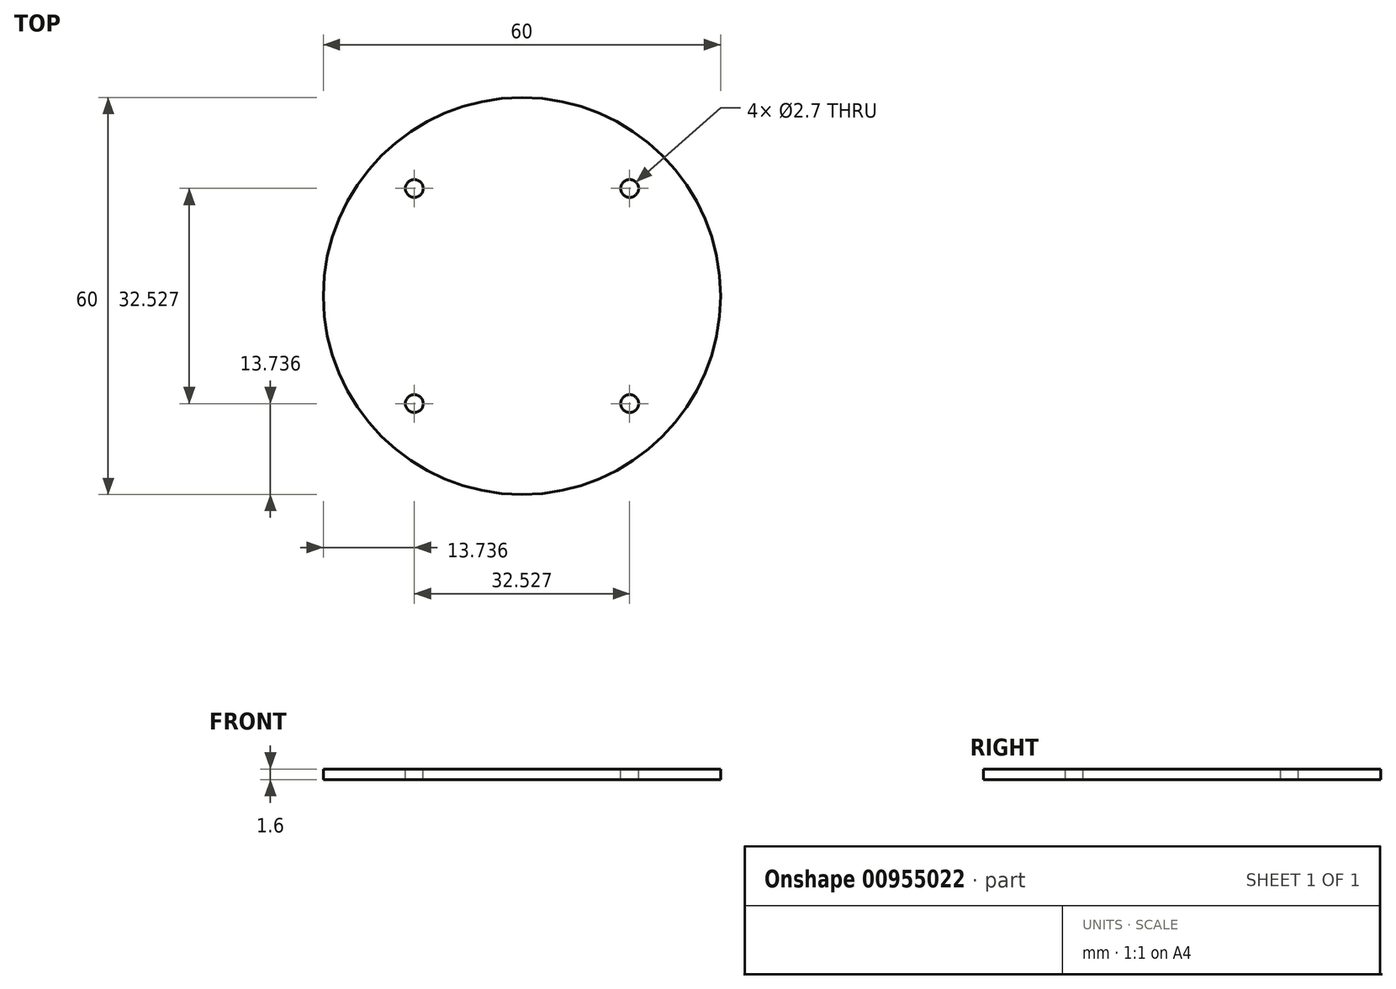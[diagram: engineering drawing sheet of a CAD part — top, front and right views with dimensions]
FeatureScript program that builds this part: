
annotation { "Feature Type Name" : "Feature", "Feature Type Description" : "" }
export const myFeature = defineFeature(function(context is Context, id is Id, definition is map)
    precondition{}
    {
        {
            var Q0;
            Q0=qCreatedBy(makeId("Top.planeOp"),FACE);
            var sketch = newSketch(context, id + "F0", { "sketchPlane" : qUnion([Q0])});
            skCircle(sketch, "E0", {"center": v(0, 0) * mm, "radius": 30 * mm});
            skSolve(sketch);
        }
        {
            var Q0;
            Q0 = qSketchRegion(id + "F0", true);
            extrude(context, id + "F1", {"entities" : qUnion([Q0]), "depth" : 1.6 * mm, "offsetDistance" : 25.4 * mm});
        }
        {
            var Q0;
            Q0=makeQuery(id+"F1.opExtrude","CAP_FACE",FACE,{"disambiguationData":[OSD([sQuery(id+"F0.wireOp",EDGE,"E0")])],"isStart":false});
            var sketch = newSketch(context, id + "F2", { "sketchPlane" : qUnion([Q0])});
            skCircle(sketch, "E1", {"center": v(-16.26, 16.26) * mm, "radius": 1.35 * mm});
            skLineSegment(sketch, "E2", {"start": v(0, 0) * mm, "end": v(-36.01, 36.01) * mm, "construction": true});
            skCircle(sketch, "E3.1.0", {"center": v(-16.26, -16.26) * mm, "radius": 1.35 * mm});
            skCircle(sketch, "E3.2.0", {"center": v(16.26, -16.26) * mm, "radius": 1.35 * mm});
            skCircle(sketch, "E3.3.0", {"center": v(16.26, 16.26) * mm, "radius": 1.35 * mm});
            skPoint(sketch, "E3.center", {"position": v(0, 0) * mm});
            skSolve(sketch);
        }
        {
            var Q0;
            Q0 = qSketchRegion(id + "F2", true);
            extrude(context, id + "F3", {"entities" : qUnion([Q0]), "operationType" : NewBodyOperationType.REMOVE, "oppositeDirection" : true, "depth" : 25 * mm, "offsetDistance" : 25 * mm});
        }
    });
